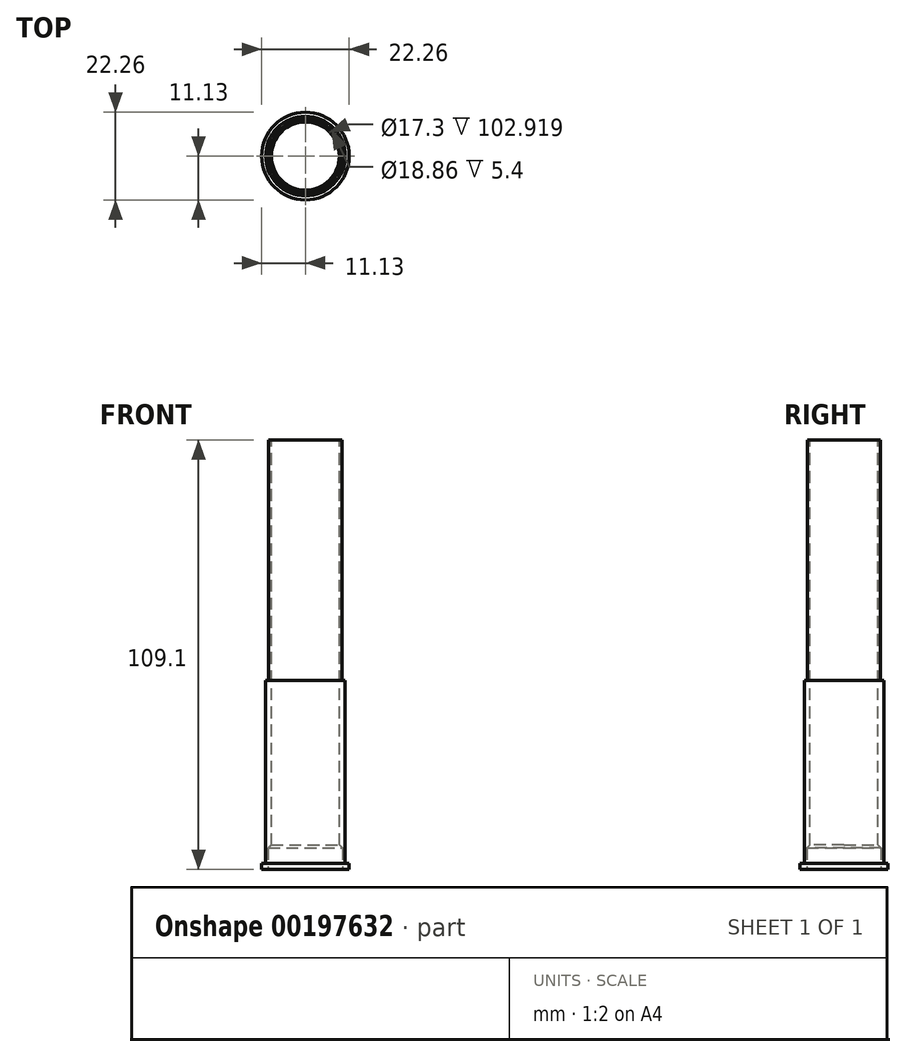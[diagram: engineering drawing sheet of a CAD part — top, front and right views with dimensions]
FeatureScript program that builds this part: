
annotation { "Feature Type Name" : "Feature", "Feature Type Description" : "" }
export const myFeature = defineFeature(function(context is Context, id is Id, definition is map)
    precondition{}
    {
        {
            var Q0;
            Q0=qCreatedBy(makeId("Right.planeOp"),FACE);
            var sketch = newSketch(context, id + "F0", { "sketchPlane" : qUnion([Q0])});
            skLineSegment(sketch, "E0", {"start": v(-9.23, 0) * mm, "end": v(-11.12, 0) * mm});
            skLineSegment(sketch, "E1", {"start": v(-11.12, 0) * mm, "end": v(-11.12, 1.37) * mm});
            skLineSegment(sketch, "E2", {"start": v(-11.12, 1.37) * mm, "end": v(-10.1, 1.37) * mm});
            skLineSegment(sketch, "E3", {"start": v(-10.1, 1.37) * mm, "end": v(-10.1, 16.34) * mm});
            skLineSegment(sketch, "E4", {"start": v(-10.1, 16.34) * mm, "end": v(-10.1, 47.95) * mm});
            skLineSegment(sketch, "E5", {"start": v(-10.1, 47.95) * mm, "end": v(-9.33, 47.95) * mm});
            skPoint(sketch, "E6.start.orphan", {"position": v(0, 47.95) * mm});
            skLineSegment(sketch, "E7", {"start": v(0, 47.95) * mm, "end": v(0, 0) * mm, "construction": true});
            skLineSegment(sketch, "E8", {"start": v(-9.33, 47.95) * mm, "end": v(-9.33, 109) * mm});
            skLineSegment(sketch, "E9", {"start": v(-9.23, 5.5) * mm, "end": v(-8.65, 5.5) * mm, "construction": true});
            skLineSegment(sketch, "E10", {"start": v(-8.65, 5.5) * mm, "end": v(-8.65, 6.08) * mm, "construction": true});
            skLineSegment(sketch, "E11", {"start": v(-9.23, 0) * mm, "end": v(-9.23, 5.5) * mm});
            skLineSegment(sketch, "E12", {"start": v(-9.33, 109) * mm, "end": v(-8.65, 109) * mm});
            skLineSegment(sketch, "E13", {"start": v(-9.23, 5.5) * mm, "end": v(-8.65, 6.08) * mm});
            skLineSegment(sketch, "E14", {"start": v(-8.65, 6.08) * mm, "end": v(-8.65, 109) * mm});
            skSolve(sketch);
        }
        {
            var Q0;
            Q0=makeQuery(id+"F0.imprint","IMPRINT",FACE,{"disambiguationData":[TD([[makeQuery(id+"F0.imprint","IMPRINT",EDGE,{"derivedFrom":sQuery(id+"F0.wireOp",EDGE,"E0")}),-1.0]])]});
            var Q1;
            Q1=sQuery(id+"F0.wireOp",EDGE,"E7");
            revolve(context, id + "F1", {"entities" : qUnion([Q0]), "axis" : qUnion([Q1]), "revolveType" : RevolveType.FULL});
        }
        {
            var Q0;
            Q0=makeQuery(id+"F1.opRevolve","SWEPT_FACE",FACE,{"disambiguationData":[OSD([sQuery(id+"F0.wireOp",EDGE,"E0")])]});
            var sketch = newSketch(context, id + "F2", { "sketchPlane" : qUnion([Q0])});
            skCircle(sketch, "E15.0", {"center": v(0, 0) * mm, "radius": 11.12 * mm});
            skCircle(sketch, "E16.0", {"center": v(0, 0) * mm, "radius": 9.23 * mm});
            skSolve(sketch);
        }
        {
            var Q0;
            Q0 = qSketchRegion(id + "F2", true);
            extrude(context, id + "F3", {"entities" : qUnion([Q0]), "operationType" : NewBodyOperationType.ADD, "depth" : .1 * mm});
        }
        {
            var Q0;
            Q0=makeQuery(id+"F3.opExtrude","CAP_FACE",FACE,{"disambiguationData":[OSD([sQuery(id+"F2.wireOp",EDGE,"E15.0"),sQuery(id+"F2.wireOp",EDGE,"E16.0")])],"isStart":false});
            var sketch = newSketch(context, id + "F4", { "sketchPlane" : qUnion([Q0])});
            skCircle(sketch, "E17", {"center": v(0, 0) * mm, "radius": 9.43 * mm});
            skSolve(sketch);
        }
        {
            var Q0;
            Q0=makeQuery(id+"F4.imprint","IMPRINT",FACE,{"disambiguationData":[TD([[makeQuery(id+"F4.imprint","IMPRINT",EDGE,{"derivedFrom":sQuery(id+"F4.wireOp",EDGE,"E17")}),1.0]])]});
            var Q1;
            Q1=makeQuery(id+"F1.opRevolve","SWEPT_FACE",FACE,{"disambiguationData":[OSD([sQuery(id+"F0.wireOp",EDGE,"E13")])]});
            extrude(context, id + "F5", {"entities" : qUnion([Q0]), "operationType" : NewBodyOperationType.REMOVE, "endBound" : BoundingType.UP_TO_SURFACE, "oppositeDirection" : true, "endBoundEntityFace" : qUnion([Q1]), "depth" : 25 * mm});
        }
    });
